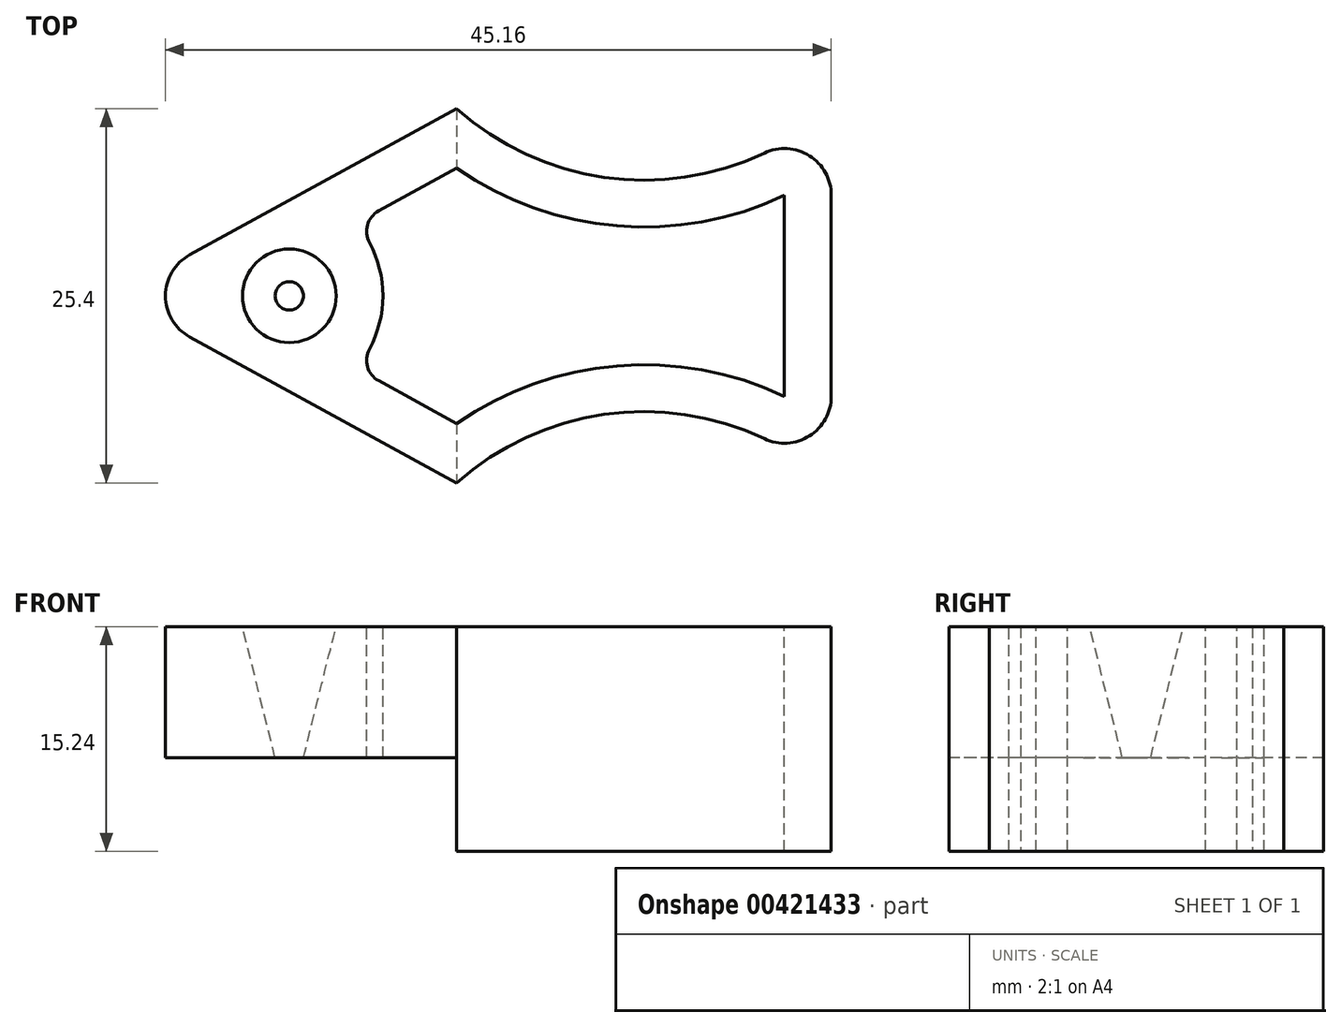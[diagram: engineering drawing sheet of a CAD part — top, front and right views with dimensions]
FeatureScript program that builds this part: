
annotation { "Feature Type Name" : "Feature", "Feature Type Description" : "" }
export const myFeature = defineFeature(function(context is Context, id is Id, definition is map)
    precondition{}
    {
        {
            var Q0;
            Q0=qCreatedBy(makeId("Top.planeOp"),FACE);
            var sketch = newSketch(context, id + "F0", { "sketchPlane" : qUnion([Q0])});
            skLineSegment(sketch, "E0.bottom", {"start": v(-25.4, 0) * mm, "end": v(-34.56, 0) * mm});
            skLineSegment(sketch, "E0.top", {"start": v(-25.4, 25.4) * mm, "end": v(-34.56, 25.4) * mm});
            skLineSegment(sketch, "E0.left", {"start": v(0, 5.88) * mm, "end": v(0, 19.52) * mm});
            skLineSegment(sketch, "E0.right", {"start": v(-34.56, 0) * mm, "end": v(-34.56, 25.4) * mm});
            skArc(sketch, "E1", {"start": v(-4.54, 3.01) * mm, "mid": v(-15.42, 4.66) * mm, "end": v(-25.4, 0) * mm});
            skArc(sketch, "E2", {"start": v(-25.4, 25.4) * mm, "mid": v(-15.42, 20.74) * mm, "end": v(-4.54, 22.39) * mm});
            skPoint(sketch, "E3.visualSharp", {"position": v(0, 25.4) * mm});
            skArc(sketch, "E3.filletArc", {"start": v(0, 19.52) * mm, "mid": v(-1.48, 22.2) * mm, "end": v(-4.54, 22.39) * mm});
            skPoint(sketch, "E4.visualSharp", {"position": v(0, 0) * mm});
            skArc(sketch, "E4.filletArc", {"start": v(-4.54, 3.01) * mm, "mid": v(-1.48, 3.2) * mm, "end": v(0, 5.88) * mm});
            skCircle(sketch, "E5", {"center": v(-36.76, 12.7) * mm, "radius": 17.04 * mm});
            skPoint(sketch, "E6", {"position": v(-34.56, 12.7) * mm});
            skSolve(sketch);
        }
        {
            var Q0;
            {var subQ0=sQuery(id+"F0.wireOp",EDGE,"E0.bottom");Q0=makeQuery(id+"F0.imprint","IMPRINT",FACE,{"disambiguationData":[TD([[makeQuery(id+"F0.imprint","IMPRINT",EDGE,{"derivedFrom":subQ0}),1.0]])]});}
            var Q1;
            {var subQ0=sQuery(id+"F0.wireOp",EDGE,"E0.bottom");Q1=makeQuery(id+"F0.imprint","IMPRINT",FACE,{"disambiguationData":[TD([[makeQuery(id+"F0.imprint","IMPRINT",EDGE,{"derivedFrom":subQ0}),-1.0]])]});}
            var Q2;
            Q2=makeQuery(id+"F0.imprint","IMPRINT",FACE,{"disambiguationData":[TD([[makeQuery(id+"F0.imprint","IMPRINT",EDGE,{"derivedFrom":sQuery(id+"F0.wireOp",EDGE,"E0.left")}),1.0]])]});
            extrude(context, id + "F1", {"entities" : qUnion([Q0, Q1, Q2]), "depth" : 15.24 * mm, "offsetDistance" : 25.4 * mm});
        }
        {
            var Q0;
            Q0=makeQuery(id+"F1.opExtrude","CAP_FACE",FACE,{"disambiguationData":[OSD([sQuery(id+"F0.wireOp",EDGE,"E0.left"),sQuery(id+"F0.wireOp",EDGE,"E1"),sQuery(id+"F0.wireOp",EDGE,"E2"),sQuery(id+"F0.wireOp",EDGE,"E3.filletArc"),sQuery(id+"F0.wireOp",EDGE,"E4.filletArc"),sQuery(id+"F0.wireOp",EDGE,"E5")])],"isStart":false});
            var sketch = newSketch(context, id + "F2", { "sketchPlane" : qUnion([Q0])});
            skCircle(sketch, "E7", {"center": v(-36.76, 12.7) * mm, "radius": 3.18 * mm});
            skSolve(sketch);
        }
        {
            var Q0;
            Q0=qSketchRegion(id+"F2",true);
            var Q1;
            Q1=makeQuery(id+"F1.opExtrude","CAP_FACE",FACE,{"disambiguationData":[OSD([sQuery(id+"F0.wireOp",EDGE,"E0.left"),sQuery(id+"F0.wireOp",EDGE,"E1"),sQuery(id+"F0.wireOp",EDGE,"E2"),sQuery(id+"F0.wireOp",EDGE,"E3.filletArc"),sQuery(id+"F0.wireOp",EDGE,"E4.filletArc"),sQuery(id+"F0.wireOp",EDGE,"E5")])],"isStart":true});
            extrude(context, id + "F3", {"entities" : qUnion([Q0]), "operationType" : NewBodyOperationType.REMOVE, "endBound" : BoundingType.UP_TO_NEXT, "oppositeDirection" : true, "endBoundEntityFace" : qUnion([Q1]), "depth" : 25.4 * mm, "hasDraft" : true, "draftAngle" : 14 * degree, "draftPullDirection" : true});
        }
        {
            var Q0;
            Q0=makeQuery(id+"F1.opExtrude","CAP_FACE",FACE,{"disambiguationData":[OSD([sQuery(id+"F0.wireOp",EDGE,"E0.left"),sQuery(id+"F0.wireOp",EDGE,"E1"),sQuery(id+"F0.wireOp",EDGE,"E2"),sQuery(id+"F0.wireOp",EDGE,"E3.filletArc"),sQuery(id+"F0.wireOp",EDGE,"E4.filletArc"),sQuery(id+"F0.wireOp",EDGE,"E5")])],"isStart":false});
            var sketch = newSketch(context, id + "F4", { "sketchPlane" : qUnion([Q0])});
            skLineSegment(sketch, "E8", {"start": v(-25.4, 0) * mm, "end": v(-43.5, 9.92) * mm});
            skLineSegment(sketch, "E9", {"start": v(-43.5, 15.48) * mm, "end": v(-25.4, 25.4) * mm});
            skPoint(sketch, "E10", {"position": v(0, 12.7) * mm});
            skPoint(sketch, "E11.visualSharp", {"position": v(-48.6, 12.7) * mm});
            skArc(sketch, "E11.filletArc", {"start": v(-43.5, 15.48) * mm, "mid": v(-45.16, 12.7) * mm, "end": v(-43.5, 9.92) * mm});
            skArc(sketch, "E12.0", {"start": v(-3.18, 5.88) * mm, "mid": v(-14.54, 7.95) * mm, "end": v(-25.4, 4.04) * mm});
            skLineSegment(sketch, "E12.1", {"start": v(-3.18, 5.88) * mm, "end": v(-3.18, 19.52) * mm});
            skArc(sketch, "E12.2", {"start": v(-25.4, 21.36) * mm, "mid": v(-14.54, 17.45) * mm, "end": v(-3.17, 19.52) * mm});
            skLineSegment(sketch, "E13", {"start": v(-25.4, 4.04) * mm, "end": v(-30.7, 6.94) * mm});
            skLineSegment(sketch, "E14", {"start": v(-25.4, 21.36) * mm, "end": v(-30.7, 18.46) * mm});
            skArc(sketch, "E15", {"start": v(-31.32, 9.09) * mm, "mid": v(-30.4, 12.7) * mm, "end": v(-31.32, 16.31) * mm});
            skPoint(sketch, "E16", {"position": v(-33.58, 12.7) * mm});
            skPoint(sketch, "E17", {"position": v(-30.4, 12.7) * mm});
            skPoint(sketch, "E18.visualSharp", {"position": v(-32.22, 7.78) * mm});
            skArc(sketch, "E18.filletArc", {"start": v(-31.32, 9.09) * mm, "mid": v(-31.45, 7.88) * mm, "end": v(-30.7, 6.94) * mm});
            skPoint(sketch, "E19.visualSharp", {"position": v(-32.22, 17.62) * mm});
            skArc(sketch, "E19.filletArc", {"start": v(-30.7, 18.46) * mm, "mid": v(-31.45, 17.52) * mm, "end": v(-31.32, 16.31) * mm});
            skSolve(sketch);
        }
        {
            var Q0;
            Q0=makeQuery(id+"F4.imprint","IMPRINT",FACE,{"disambiguationData":[TD([[makeQuery(id+"F4.imprint","IMPRINT",EDGE,{"derivedFrom":sQuery(id+"F4.wireOp",EDGE,"E12.0")}),-1.0]])]});
            var Q1;
            Q1=makeQuery(id+"F4.imprint","IMPRINT",FACE,{"disambiguationData":[TD([[makeQuery(id+"F4.imprint","IMPRINT",EDGE,{"derivedFrom":sQuery(id+"F4.wireOp",EDGE,"E8")}),1.0]])]});
            extrude(context, id + "F5", {"entities" : qUnion([Q0, Q1]), "operationType" : NewBodyOperationType.REMOVE, "endBound" : BoundingType.THROUGH_ALL, "oppositeDirection" : true, "depth" : 25.4 * mm});
        }
        {
            var Q0;
            Q0=qCreatedBy(makeId("Front.planeOp"),FACE);
            var sketch = newSketch(context, id + "F6", { "sketchPlane" : qUnion([Q0])});
            skLineSegment(sketch, "E20.bottom", {"start": v(-25.4, 0) * mm, "end": v(-63.5, 0) * mm});
            skLineSegment(sketch, "E20.top", {"start": v(-25.4, 6.35) * mm, "end": v(-63.5, 6.35) * mm});
            skLineSegment(sketch, "E20.left", {"start": v(-25.4, 0) * mm, "end": v(-25.4, 6.35) * mm});
            skLineSegment(sketch, "E20.right", {"start": v(-63.5, 0) * mm, "end": v(-63.5, 6.35) * mm});
            skSolve(sketch);
        }
        {
            var Q0;
            Q0=makeQuery(id+"F6.imprint","IMPRINT",FACE,{"disambiguationData":[TD([[makeQuery(id+"F6.imprint","IMPRINT",EDGE,{"derivedFrom":sQuery(id+"F6.wireOp",EDGE,"E20.bottom")}),-1.0]])]});
            extrude(context, id + "F7", {"entities" : qUnion([Q0]), "operationType" : NewBodyOperationType.REMOVE, "endBound" : BoundingType.THROUGH_ALL, "oppositeDirection" : true, "depth" : 25.4 * mm});
        }
    });
